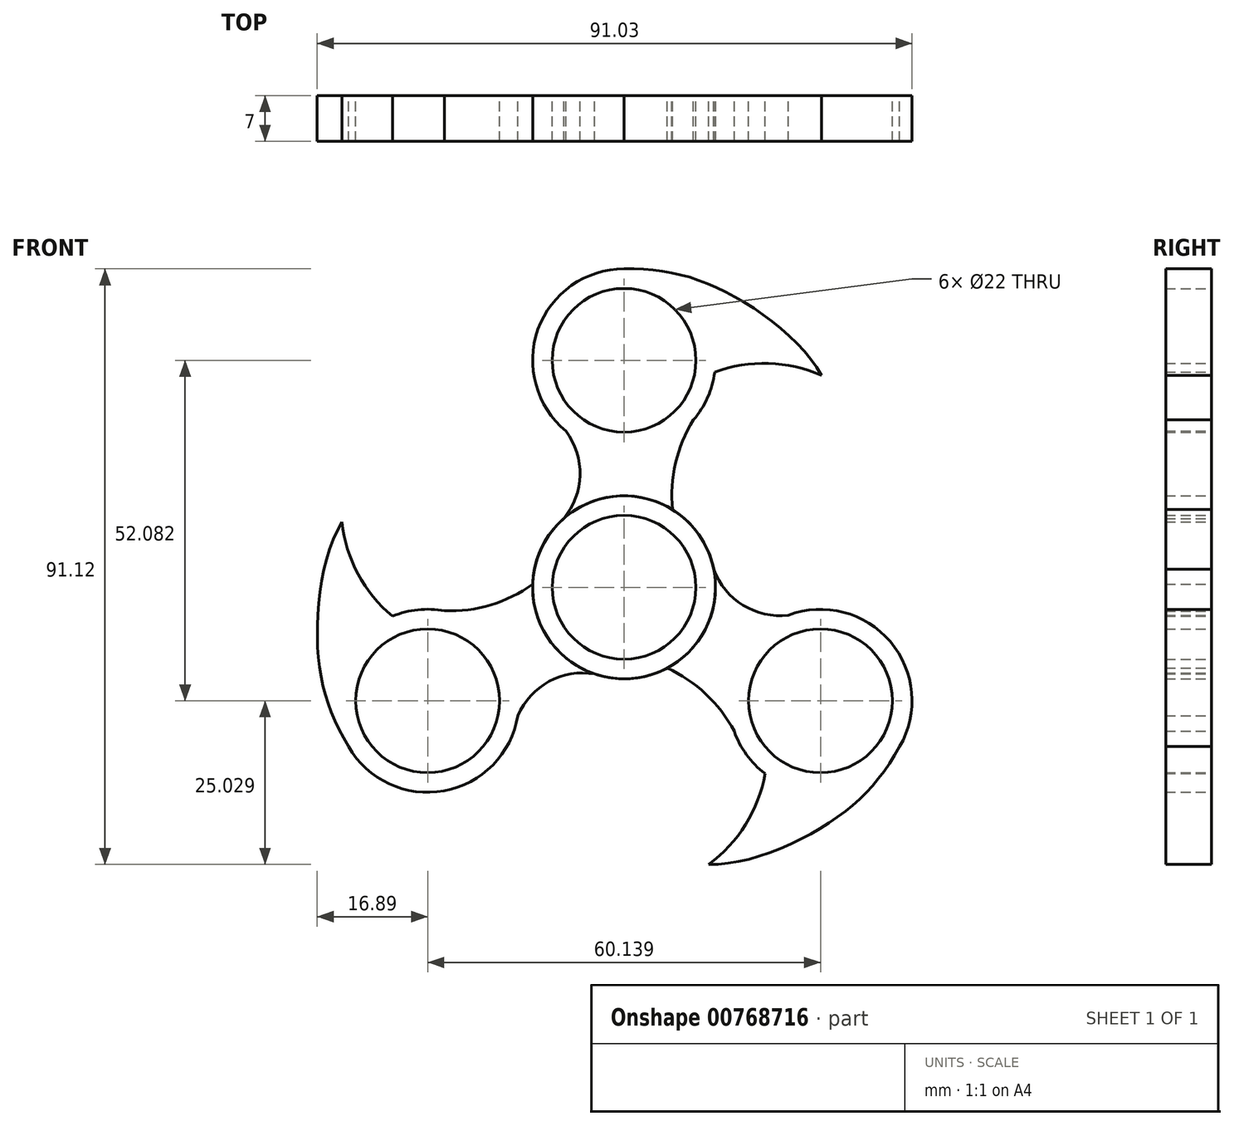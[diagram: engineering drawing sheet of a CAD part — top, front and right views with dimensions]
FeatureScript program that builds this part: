
annotation { "Feature Type Name" : "Feature", "Feature Type Description" : "" }
export const myFeature = defineFeature(function(context is Context, id is Id, definition is map)
    precondition{}
    {
        {
            var Q0;
            Q0=qCreatedBy(makeId("Front.planeOp"),FACE);
            var sketch = newSketch(context, id + "F0", { "sketchPlane" : qUnion([Q0])});
            skCircle(sketch, "E0", {"center": v(0, 0) * mm, "radius": 11 * mm});
            skCircle(sketch, "E1", {"center": v(0, 0) * mm, "radius": 14 * mm});
            skCircle(sketch, "E2", {"center": v(0, 34.72) * mm, "radius": 14 * mm});
            skCircle(sketch, "E3", {"center": v(0, 34.72) * mm, "radius": 11 * mm});
            skArc(sketch, "E4", {"start": v(-9.24, 10.52) * mm, "mid": v(-6.74, 17.15) * mm, "end": v(-8.89, 23.9) * mm});
            skArc(sketch, "E5", {"start": v(10.63, 25.61) * mm, "mid": v(7.88, 19.02) * mm, "end": v(7.4, 11.88) * mm});
            skFitSpline(sketch, "E6", {"points": [v(0, 48.72) * mm, v(15.3, 45.3) * mm, v(30.23, 32.4) * mm], "startDerivative": vector(35.74, 0.51) * mm, "endDerivative": vector(15.6, -29.04) * mm});
            skArc(sketch, "E7", {"start": v(30.23, 32.4) * mm, "mid": v(22.1, 34.26) * mm, "end": v(13.88, 32.93) * mm});
            skSolve(sketch);
        }
        {
            var Q0;
            Q0=makeQuery(id+"F0.imprint","IMPRINT",FACE,{"disambiguationData":[TD([[makeQuery(id+"F0.imprint","IMPRINT",EDGE,{"derivedFrom":sQuery(id+"F0.wireOp",EDGE,"E3")}),-1.0]])]});
            var Q1;
            {var subQ0=sQuery(id+"F0.wireOp",EDGE,"E4");Q1=makeQuery(id+"F0.imprint","IMPRINT",FACE,{"disambiguationData":[TD([[makeQuery(id+"F0.imprint","IMPRINT",EDGE,{"derivedFrom":subQ0}),-1.0]])]});}
            var Q2;
            Q2=makeQuery(id+"F0.imprint","IMPRINT",FACE,{"disambiguationData":[TD([[makeQuery(id+"F0.imprint","IMPRINT",EDGE,{"derivedFrom":sQuery(id+"F0.wireOp",EDGE,"E0")}),-1.0]])]});
            var Q3;
            {var subQ0=sQuery(id+"F0.wireOp",EDGE,"E6");Q3=makeQuery(id+"F0.imprint","IMPRINT",FACE,{"disambiguationData":[TD([[makeQuery(id+"F0.imprint","IMPRINT",EDGE,{"derivedFrom":subQ0}),-1.0]])]});}
            extrude(context, id + "F1", {"entities" : qUnion([Q0, Q1, Q2, Q3]), "depth" : 7 * mm, "offsetDistance" : 25.4 * mm});
        }
        {
            var Q0;
            Q0=makeQuery(id+"F1.opExtrude","SWEPT_BODY",BODY,{"disambiguationData":[OSD([sQuery(id+"F0.wireOp",EDGE,"E0"),sQuery(id+"F0.wireOp",EDGE,"E1"),sQuery(id+"F0.wireOp",EDGE,"E2"),sQuery(id+"F0.wireOp",EDGE,"E3"),sQuery(id+"F0.wireOp",EDGE,"E4"),sQuery(id+"F0.wireOp",EDGE,"E5"),sQuery(id+"F0.wireOp",EDGE,"E6"),sQuery(id+"F0.wireOp",EDGE,"E7")])]});
            var Q1;
            Q1=makeQuery(id+"F1.opExtrude","CAP_EDGE",EDGE,{"disambiguationData":[OSD([sQuery(id+"F0.wireOp",EDGE,"E0")])],"isStart":false});
            circularPattern(context, id + "F2", {"entities" : qUnion([Q0]), "axis" : qUnion([Q1]), "angle" : 360 * degree, "instanceCount" : 3, "equalSpace" : true});
        }
    });
